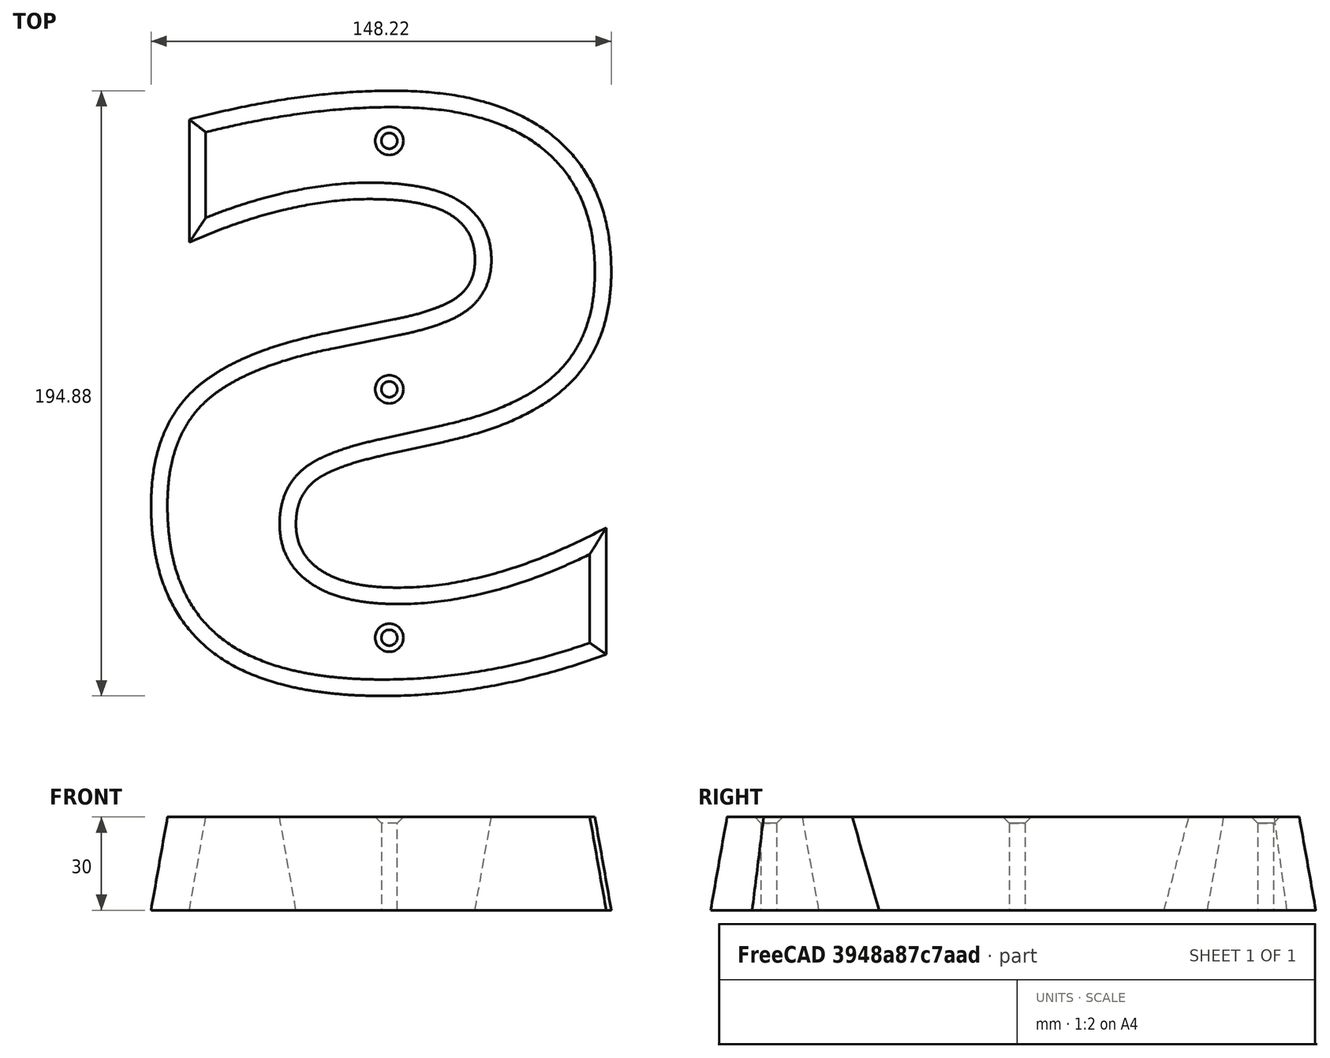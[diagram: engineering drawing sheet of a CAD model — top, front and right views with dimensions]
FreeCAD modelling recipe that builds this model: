
FCSTD DOCUMENT  (FreeCAD 0.21RUnknown)
Label: s-mirror
License: All rights reserved
LicenseURL: https://en.wikipedia.org/wiki/All_rights_reserved
objects: Part::Cylinder×3, Part::Cut×3, Part::Offset2D×2, Part::Part2DObjectPython×1, Part::Mirroring×1, Sketcher::SketchObject×1, Part::Loft×1, Part::Chamfer×1
note: 13 computed .brp shape members not serialized (recipe doc carries the construction recipe); baked Part::Feature solids carry a one-line shape summary decoded from their .brp

FEATURE [Part::Part2DObjectPython] ShapeString  # Draft 2D object (typed FeaturePython)
  FontFile = /nix/var/nix/profiles/system/sw/share/X11/fonts/DejaVuSans-Bold.ttf
  MakeFace = false
  Size = 200
  String = S
  Tracking = 0
FEATURE [Part::Mirroring] Mirror  label="ShapeString (mirrored)"
  Base = (0,0,0)
  Normal = (1,0,0)
  Source = -> ShapeString
FEATURE [Sketcher::SketchObject] Sketch  label="s-Sketch"
  FullyConstrained = false
  sketch-geometry (92):
    g0: LineSegment StartX=-154.404 StartY=181.888 StartZ=0 EndX=-154.404 EndY=142.282 EndZ=0
    g1: ArcOfCircle CenterX=-72.4025 CenterY=-127.848 CenterZ=0 NormalX=0 NormalY=0 NormalZ=1 AngleXU=0 Radius=320.406 StartAngle=1.77565 EndAngle=1.82961
    g2: ArcOfCircle CenterX=-83.2735 CenterY=-75.5247 CenterZ=0 NormalX=0 NormalY=0 NormalZ=1 AngleXU=0 Radius=266.966 StartAngle=1.7109 EndAngle=1.77565
    g3: ArcOfCircle CenterX=-86.4858 CenterY=-51.8715 CenterZ=0 NormalX=0 NormalY=0 NormalZ=1 AngleXU=0 Radius=243.096 StartAngle=1.64569 EndAngle=1.7114
    g4: ArcOfCircle CenterX=-88.7164 CenterY=-22.1421 CenterZ=0 NormalX=0 NormalY=0 NormalZ=1 AngleXU=0 Radius=213.283 StartAngle=1.5708 EndAngle=1.64569
    g5: ArcOfCircle CenterX=-88.7164 CenterY=52.2641 CenterZ=0 NormalX=0 NormalY=0 NormalZ=1 AngleXU=0 Radius=138.877 StartAngle=1.46144 EndAngle=1.5708
    g6: ArcOfCircle CenterX=-83.1389 CenterY=103.065 CenterZ=0 NormalX=0 NormalY=0 NormalZ=1 AngleXU=0 Radius=87.7708 StartAngle=1.28867 EndAngle=1.46144
    g7: ArcOfCircle CenterX=-78.3313 CenterY=119.651 CenterZ=0 NormalX=0 NormalY=0 NormalZ=1 AngleXU=0 Radius=70.5019 StartAngle=1.11122 EndAngle=1.28867
    g8: ArcOfCircle CenterX=-70.6109 CenterY=135.25 CenterZ=0 NormalX=0 NormalY=0 NormalZ=1 AngleXU=0 Radius=53.0969 StartAngle=0.876058 EndAngle=1.11122
    g9: ArcOfCircle CenterX=-67.6851 CenterY=138.761 CenterZ=0 NormalX=0 NormalY=0 NormalZ=1 AngleXU=0 Radius=48.5266 StartAngle=0.638556 EndAngle=0.876058
    g10: ArcOfCircle CenterX=-67.0907 CenterY=139.202 CenterZ=0 NormalX=0 NormalY=0 NormalZ=1 AngleXU=0 Radius=47.7863 StartAngle=0.39741 EndAngle=0.638556
    g11: ArcOfCircle CenterX=-72.8538 CenterY=136.783 CenterZ=0 NormalX=0 NormalY=0 NormalZ=1 AngleXU=0 Radius=54.0366 StartAngle=0.162609 EndAngle=0.39741
    g12: ArcOfCircle CenterX=-96.7123 CenterY=132.869 CenterZ=0 NormalX=0 NormalY=0 NormalZ=1 AngleXU=0 Radius=78.214 StartAngle=-9e-16 EndAngle=0.162609
    g13: ArcOfCircle CenterX=-88.6496 CenterY=132.869 CenterZ=0 NormalX=0 NormalY=0 NormalZ=1 AngleXU=0 Radius=70.1513 StartAngle=6.13716 EndAngle=6.28319
    g14: ArcOfCircle CenterX=-68.7218 CenterY=129.938 CenterZ=0 NormalX=0 NormalY=0 NormalZ=1 AngleXU=0 Radius=50.0091 StartAngle=5.93268 EndAngle=6.13716
    g15: ArcOfCircle CenterX=-63.2383 CenterY=127.934 CenterZ=0 NormalX=0 NormalY=0 NormalZ=1 AngleXU=0 Radius=44.1707 StartAngle=5.72359 EndAngle=5.93268
    g16: ArcOfCircle CenterX=-61.6232 CenterY=126.922 CenterZ=0 NormalX=0 NormalY=0 NormalZ=1 AngleXU=0 Radius=42.2648 StartAngle=5.50514 EndAngle=5.72359
    g17: ArcOfCircle CenterX=-65.5059 CenterY=130.769 CenterZ=0 NormalX=0 NormalY=0 NormalZ=1 AngleXU=0 Radius=47.731 StartAngle=5.29096 EndAngle=5.50482
    g18: ArcOfCircle CenterX=-78.9203 CenterY=151.308 CenterZ=0 NormalX=0 NormalY=0 NormalZ=1 AngleXU=0 Radius=72.2623 StartAngle=5.14939 EndAngle=5.29096
    g19: ArcOfCircle CenterX=-87.2378 CenterY=169.114 CenterZ=0 NormalX=0 NormalY=0 NormalZ=1 AngleXU=0 Radius=91.9148 StartAngle=5.00977 EndAngle=5.14939
    g20: ArcOfCircle CenterX=-103.93 CenterY=223.579 CenterZ=0 NormalX=0 NormalY=0 NormalZ=1 AngleXU=0 Radius=148.88 StartAngle=4.92348 EndAngle=5.00977
    g21: LineSegment StartX=-91.4849 StartY=73.8339 StartZ=0 EndX=-72.7349 EndY=78.0034 EndZ=0
    g22: ArcOfCircle CenterX=-56.162 CenterY=-85.588 CenterZ=0 NormalX=0 NormalY=0 NormalZ=1 AngleXU=-3.14159 Radius=163.288 StartAngle=4.93044 EndAngle=4.97589
    g23: ArcOfCircle CenterX=-78.6317 CenterY=-2.29803 CenterZ=0 NormalX=0 NormalY=0 NormalZ=1 AngleXU=-3.14159 Radius=77.0206 StartAngle=4.97589 EndAngle=5.07221
    g24: ArcOfCircle CenterX=-86.261 CenterY=17.9823 CenterZ=0 NormalX=0 NormalY=0 NormalZ=1 AngleXU=-3.14159 Radius=55.3527 StartAngle=5.07221 EndAngle=5.1216
    g25: ArcOfCircle CenterX=-94.4489 CenterY=36.8616 CenterZ=0 NormalX=0 NormalY=0 NormalZ=1 AngleXU=-3.14159 Radius=34.7742 StartAngle=5.1216 EndAngle=5.20021
    g26: ArcOfCircle CenterX=-97.8393 CenterY=43.2514 CenterZ=0 NormalX=0 NormalY=0 NormalZ=1 AngleXU=-3.14159 Radius=27.5408 StartAngle=5.20021 EndAngle=5.27789
    g27: ArcOfCircle CenterX=-103.946 CenterY=52.874 CenterZ=0 NormalX=0 NormalY=0 NormalZ=1 AngleXU=-3.14159 Radius=16.1439 StartAngle=5.27789 EndAngle=5.41029
    g28: ArcOfCircle CenterX=-104.376 CenterY=53.3693 CenterZ=0 NormalX=0 NormalY=0 NormalZ=1 AngleXU=-3.14159 Radius=15.488 StartAngle=5.40957 EndAngle=5.6451
    g29: ArcOfCircle CenterX=-104.632 CenterY=53.5589 CenterZ=0 NormalX=0 NormalY=0 NormalZ=1 AngleXU=-3.14159 Radius=15.1697 StartAngle=5.6451 EndAngle=5.88552
    g30: ArcOfCircle CenterX=-102.87 CenterY=52.8188 CenterZ=0 NormalX=0 NormalY=0 NormalZ=1 AngleXU=-3.14159 Radius=17.081 StartAngle=5.88552 EndAngle=6.11984
    g31: ArcOfCircle CenterX=-95.4893 CenterY=51.6023 CenterZ=0 NormalX=0 NormalY=0 NormalZ=1 AngleXU=-3.14159 Radius=24.5611 StartAngle=6.11984 EndAngle=6.28319
    g32: ArcOfCircle CenterX=-99.5529 CenterY=51.6023 CenterZ=0 NormalX=0 NormalY=0 NormalZ=1 AngleXU=-3.14159 Radius=20.4974 StartAngle=-9e-16 EndAngle=0.221382
    g33: ArcOfCircle CenterX=-104.124 CenterY=50.5736 CenterZ=0 NormalX=0 NormalY=0 NormalZ=1 AngleXU=-3.14159 Radius=15.8122 StartAngle=0.221382 EndAngle=0.507568
    g34: ArcOfCircle CenterX=-103.996 CenterY=50.6444 CenterZ=0 NormalX=0 NormalY=0 NormalZ=1 AngleXU=-3.14159 Radius=15.9579 StartAngle=0.507568 EndAngle=0.793047
    g35: ArcOfCircle CenterX=-100.328 CenterY=54.369 CenterZ=0 NormalX=0 NormalY=0 NormalZ=1 AngleXU=-3.14159 Radius=21.1854 StartAngle=0.793047 EndAngle=1.00872
    g36: ArcOfCircle CenterX=-97.6855 CenterY=58.6 CenterZ=0 NormalX=0 NormalY=0 NormalZ=1 AngleXU=-3.14159 Radius=26.1741 StartAngle=1.00943 EndAngle=1.22095
    g37: ArcOfCircle CenterX=-92.5595 CenterY=72.6496 CenterZ=0 NormalX=0 NormalY=0 NormalZ=1 AngleXU=-3.14159 Radius=41.1296 StartAngle=1.22095 EndAngle=1.35586
    g38: ArcOfCircle CenterX=-90.0842 CenterY=83.988 CenterZ=0 NormalX=0 NormalY=0 NormalZ=1 AngleXU=-3.14159 Radius=52.735 StartAngle=1.35586 EndAngle=1.48939
    g39: ArcOfCircle CenterX=-87.3322 CenterY=117.719 CenterZ=0 NormalX=0 NormalY=0 NormalZ=1 AngleXU=-3.14159 Radius=86.5777 StartAngle=1.48939 EndAngle=1.5708
    g40: ArcOfCircle CenterX=-87.3322 CenterY=135.782 CenterZ=0 NormalX=0 NormalY=0 NormalZ=1 AngleXU=-3.14159 Radius=104.641 StartAngle=1.5708 EndAngle=1.72785
    g41: ArcOfCircle CenterX=-91.5759 CenterY=162.581 CenterZ=0 NormalX=0 NormalY=0 NormalZ=1 AngleXU=-3.14159 Radius=131.774 StartAngle=1.72785 EndAngle=1.85265
    g42: ArcOfCircle CenterX=-98.6888 CenterY=187.069 CenterZ=0 NormalX=0 NormalY=0 NormalZ=1 AngleXU=-3.14159 Radius=157.274 StartAngle=1.85279 EndAngle=1.97275
    g43: ArcOfCircle CenterX=-121.083 CenterY=239.748 CenterZ=0 NormalX=0 NormalY=0 NormalZ=1 AngleXU=-3.14159 Radius=214.516 StartAngle=1.97275 EndAngle=2.06075
    g44: LineSegment StartX=-20.1342 StartY=9.62248 StartZ=0 EndX=-20.1342 EndY=50.4698 EndZ=0
    g45: ArcOfCircle CenterX=-100.994 CenterY=229.172 CenterZ=0 NormalX=0 NormalY=0 NormalZ=1 AngleXU=0 Radius=233.967 StartAngle=4.98535 EndAngle=5.06527
    g46: ArcOfCircle CenterX=-95.399 CenterY=209.186 CenterZ=0 NormalX=0 NormalY=0 NormalZ=1 AngleXU=0 Radius=213.212 StartAngle=4.89765 EndAngle=4.98535
    g47: ArcOfCircle CenterX=-92.8896 CenterY=195.31 CenterZ=0 NormalX=0 NormalY=0 NormalZ=1 AngleXU=0 Radius=199.111 StartAngle=4.80751 EndAngle=4.8981
    g48: ArcOfCircle CenterX=-91.9883 CenterY=185.862 CenterZ=0 NormalX=0 NormalY=0 NormalZ=1 AngleXU=0 Radius=189.621 StartAngle=4.71239 EndAngle=4.80751
    g49: ArcOfCircle CenterX=-91.9883 CenterY=174.795 CenterZ=0 NormalX=0 NormalY=0 NormalZ=1 AngleXU=0 Radius=178.553 StartAngle=4.66266 EndAngle=4.71239
    g50: ArcOfCircle CenterX=-94.0407 CenterY=133.559 CenterZ=0 NormalX=0 NormalY=0 NormalZ=1 AngleXU=0 Radius=137.267 StartAngle=4.59798 EndAngle=4.66266
    g51: ArcOfCircle CenterX=-95.9736 CenterY=116.739 CenterZ=0 NormalX=0 NormalY=0 NormalZ=1 AngleXU=0 Radius=120.335 StartAngle=4.53328 EndAngle=4.59798
    g52: ArcOfCircle CenterX=-100.933 CenterY=89.3496 CenterZ=0 NormalX=0 NormalY=0 NormalZ=1 AngleXU=0 Radius=92.501 StartAngle=4.44913 EndAngle=4.53328
    g53: ArcOfCircle CenterX=-105.006 CenterY=74.2344 CenterZ=0 NormalX=0 NormalY=0 NormalZ=1 AngleXU=0 Radius=76.8464 StartAngle=4.2789 EndAngle=4.44913
    g54: ArcOfCircle CenterX=-115.832 CenterY=50.8464 CenterZ=0 NormalX=0 NormalY=0 NormalZ=1 AngleXU=0 Radius=51.0746 StartAngle=4.02354 EndAngle=4.2789
    g55: ArcOfCircle CenterX=-119.371 CenterY=46.564 CenterZ=0 NormalX=0 NormalY=0 NormalZ=1 AngleXU=0 Radius=45.5189 StartAngle=3.76158 EndAngle=4.02377
    g56: ArcOfCircle CenterX=-116.053 CenterY=48.9329 CenterZ=0 NormalX=0 NormalY=0 NormalZ=1 AngleXU=0 Radius=49.5961 StartAngle=3.52072 EndAngle=3.76158
    g57: ArcOfCircle CenterX=-109.79 CenterY=51.4279 CenterZ=0 NormalX=0 NormalY=0 NormalZ=1 AngleXU=0 Radius=56.3372 StartAngle=3.40486 EndAngle=3.52072
    g58: ArcOfCircle CenterX=-97.7599 CenterY=54.6703 CenterZ=0 NormalX=0 NormalY=0 NormalZ=1 AngleXU=0 Radius=68.7968 StartAngle=3.30994 EndAngle=3.40486
    g59: ArcOfCircle CenterX=-89.3288 CenterY=56.1032 CenterZ=0 NormalX=0 NormalY=0 NormalZ=1 AngleXU=0 Radius=77.3488 StartAngle=3.21544 EndAngle=3.30994
    g60: ArcOfCircle CenterX=-67.7259 CenterY=57.7013 CenterZ=0 NormalX=0 NormalY=0 NormalZ=1 AngleXU=0 Radius=99.0107 StartAngle=3.14159 EndAngle=3.21544
    g61: ArcOfCircle CenterX=-90.033 CenterY=57.7013 CenterZ=0 NormalX=0 NormalY=0 NormalZ=1 AngleXU=0 Radius=76.7036 StartAngle=3.00239 EndAngle=3.14159
    g62: ArcOfCircle CenterX=-115.25 CenterY=61.2344 CenterZ=0 NormalX=0 NormalY=0 NormalZ=1 AngleXU=0 Radius=51.2406 StartAngle=2.79443 EndAngle=3.00239
    g63: ArcOfCircle CenterX=-122.61 CenterY=63.8975 CenterZ=0 NormalX=0 NormalY=0 NormalZ=1 AngleXU=0 Radius=43.4135 StartAngle=2.58012 EndAngle=2.79443
    g64: ArcOfCircle CenterX=-126.312 CenterY=66.2259 CenterZ=0 NormalX=0 NormalY=0 NormalZ=1 AngleXU=0 Radius=39.0402 StartAngle=2.34203 EndAngle=2.58012
    g65: ArcOfCircle CenterX=-124.393 CenterY=64.2517 CenterZ=0 NormalX=0 NormalY=0 NormalZ=1 AngleXU=0 Radius=41.7935 StartAngle=2.2246 EndAngle=2.34203
    g66: ArcOfCircle CenterX=-116.78 CenterY=54.3163 CenterZ=0 NormalX=0 NormalY=0 NormalZ=1 AngleXU=0 Radius=54.3101 StartAngle=2.13418 EndAngle=2.2246
    g67: ArcOfCircle CenterX=-112.344 CenterY=47.2934 CenterZ=0 NormalX=0 NormalY=0 NormalZ=1 AngleXU=0 Radius=62.6168 StartAngle=2.04409 EndAngle=2.13418
    g68: ArcOfCircle CenterX=-102.724 CenterY=28.5093 CenterZ=0 NormalX=0 NormalY=0 NormalZ=1 AngleXU=0 Radius=83.7208 StartAngle=1.97669 EndAngle=2.04409
    g69: ArcOfCircle CenterX=-93.9943 CenterY=8.19599 CenterZ=0 NormalX=0 NormalY=0 NormalZ=1 AngleXU=0 Radius=105.831 StartAngle=1.84444 EndAngle=1.97669
    g70: ArcOfCircle CenterX=-72.263 CenterY=-69.226 CenterZ=0 NormalX=0 NormalY=0 NormalZ=1 AngleXU=0 Radius=186.245 StartAngle=1.76922 EndAngle=1.84444
    g71: LineSegment StartX=-88.3389 StartY=117.525 StartZ=0 EndX=-108.977 EndY=113.364 EndZ=0
    g72: ArcOfCircle CenterX=-116.046 CenterY=252.222 CenterZ=0 NormalX=0 NormalY=0 NormalZ=1 AngleXU=-3.14159 Radius=137.517 StartAngle=1.77366 EndAngle=1.82055
    g73: ArcOfCircle CenterX=-99.2236 CenterY=186.273 CenterZ=0 NormalX=0 NormalY=0 NormalZ=1 AngleXU=-3.14159 Radius=69.456 StartAngle=1.82055 EndAngle=1.91332
    g74: ArcOfCircle CenterX=-92.9649 CenterY=168.721 CenterZ=0 NormalX=0 NormalY=0 NormalZ=1 AngleXU=-3.14159 Radius=50.8215 StartAngle=1.91332 EndAngle=2.00044
    g75: ArcOfCircle CenterX=-80.315 CenterY=141.113 CenterZ=0 NormalX=0 NormalY=0 NormalZ=1 AngleXU=-3.14159 Radius=20.4533 StartAngle=2.00044 EndAngle=2.21621
    g76: ArcOfCircle CenterX=-76.9918 CenterY=136.658 CenterZ=0 NormalX=0 NormalY=0 NormalZ=1 AngleXU=-3.14159 Radius=14.8956 StartAngle=2.21789 EndAngle=2.44093
    g77: ArcOfCircle CenterX=-75.4462 CenterY=135.354 CenterZ=0 NormalX=0 NormalY=0 NormalZ=1 AngleXU=-3.14159 Radius=12.8736 StartAngle=2.44093 EndAngle=2.69864
    g78: ArcOfCircle CenterX=-76.1169 CenterY=135.672 CenterZ=0 NormalX=0 NormalY=0 NormalZ=1 AngleXU=-3.14159 Radius=13.616 StartAngle=2.69864 EndAngle=2.95292
    g79: ArcOfCircle CenterX=-80.8115 CenterY=136.569 CenterZ=0 NormalX=0 NormalY=0 NormalZ=1 AngleXU=-3.14159 Radius=18.3954 StartAngle=2.95292 EndAngle=3.14159
    g80: ArcOfCircle CenterX=-84.0066 CenterY=136.569 CenterZ=0 NormalX=0 NormalY=0 NormalZ=1 AngleXU=-3.14159 Radius=21.5905 StartAngle=3.14159 EndAngle=3.35291
    g81: ArcOfCircle CenterX=-77.826 CenterY=137.895 CenterZ=0 NormalX=0 NormalY=0 NormalZ=1 AngleXU=-3.14159 Radius=15.2693 StartAngle=3.35291 EndAngle=3.6506
    g82: ArcOfCircle CenterX=-77.2817 CenterY=138.198 CenterZ=0 NormalX=0 NormalY=0 NormalZ=1 AngleXU=-3.14159 Radius=14.646 StartAngle=3.6506 EndAngle=3.95183
    g83: ArcOfCircle CenterX=-80.0331 CenterY=135.307 CenterZ=0 NormalX=0 NormalY=0 NormalZ=1 AngleXU=-3.14159 Radius=18.6374 StartAngle=3.95183 EndAngle=4.18923
    g84: ArcOfCircle CenterX=-83.3648 CenterY=129.53 CenterZ=0 NormalX=0 NormalY=0 NormalZ=1 AngleXU=-3.14159 Radius=25.3058 StartAngle=4.18923 EndAngle=4.41057
    g85: ArcOfCircle CenterX=-90.0743 CenterY=107.979 CenterZ=0 NormalX=0 NormalY=0 NormalZ=1 AngleXU=-3.14159 Radius=47.8773 StartAngle=4.41057 EndAngle=4.52791
    g86: ArcOfCircle CenterX=-93.0401 CenterY=92.0853 CenterZ=0 NormalX=0 NormalY=0 NormalZ=1 AngleXU=-3.14159 Radius=64.0455 StartAngle=4.52791 EndAngle=4.64629
    g87: ArcOfCircle CenterX=-96.3926 CenterY=41.4375 CenterZ=0 NormalX=0 NormalY=0 NormalZ=1 AngleXU=-3.14159 Radius=114.804 StartAngle=4.64629 EndAngle=4.71239
    g88: ArcOfCircle CenterX=-96.3926 CenterY=51.8575 CenterZ=0 NormalX=0 NormalY=0 NormalZ=1 AngleXU=-3.14159 Radius=104.384 StartAngle=4.71239 EndAngle=4.84693
    g89: ArcOfCircle CenterX=-91.6103 CenterY=16.527 CenterZ=0 NormalX=0 NormalY=0 NormalZ=1 AngleXU=-3.14159 Radius=140.037 StartAngle=4.84693 EndAngle=4.94729
    g90: ArcOfCircle CenterX=-88.3502 CenterY=2.54692 CenterZ=0 NormalX=0 NormalY=0 NormalZ=1 AngleXU=-3.14159 Radius=154.392 StartAngle=4.94675 EndAngle=5.05036
    g91: ArcOfCircle CenterX=-75.2346 CenterY=-34.7704 CenterZ=0 NormalX=0 NormalY=0 NormalZ=1 AngleXU=-3.14159 Radius=193.947 StartAngle=5.05036 EndAngle=5.13287
  constraints (94):
    c: Vertical(g0)
    c: Coincident(g0,g1)
    c: Coincident(g1,g2)
    c: Coincident(g2,g3)
    c: Coincident(g3,g4)
    c: Coincident(g4,g5)
    c: Coincident(g5,g6)
    c: Coincident(g6,g7)
    c: Coincident(g7,g8)
    c: Coincident(g8,g9)
    c: Coincident(g9,g10)
    c: Coincident(g10,g11)
    c: Coincident(g11,g12)
    c: Coincident(g12,g13)
    c: Coincident(g13,g14)
    c: Coincident(g14,g15)
    c: Coincident(g15,g16)
    c: Coincident(g16,g17)
    c: Coincident(g17,g18)
    c: Coincident(g18,g19)
    c: Coincident(g19,g20)
    c: Coincident(g20,g21)
    c: Coincident(g21,g22)
    c: Coincident(g22,g23)
    c: Coincident(g23,g24)
    c: Coincident(g24,g25)
    c: Coincident(g25,g26)
    c: Coincident(g26,g27)
    c: Coincident(g27,g28)
    c: Coincident(g28,g29)
    c: Coincident(g29,g30)
    c: Coincident(g30,g31)
    c: Coincident(g31,g32)
    c: Coincident(g32,g33)
    c: Coincident(g33,g34)
    c: Coincident(g34,g35)
    c: Coincident(g35,g36)
    c: Coincident(g36,g37)
    c: Coincident(g37,g38)
    c: Coincident(g38,g39)
    c: Coincident(g39,g40)
    c: Coincident(g40,g41)
    c: Coincident(g41,g42)
    c: Coincident(g42,g43)
    c: Coincident(g43,g44)
    c: Vertical(g44)
    c: Coincident(g44,g45)
    c: Coincident(g45,g46)
    c: Coincident(g46,g47)
    c: Coincident(g47,g48)
    c: Coincident(g48,g49)
    c: Coincident(g49,g50)
    c: Coincident(g50,g51)
    c: Coincident(g51,g52)
    c: Coincident(g52,g53)
    c: Coincident(g53,g54)
    c: Coincident(g54,g55)
    c: Coincident(g55,g56)
    c: Coincident(g56,g57)
    c: Coincident(g57,g58)
    c: Coincident(g58,g59)
    c: Coincident(g59,g60)
    c: Coincident(g60,g61)
    c: Coincident(g61,g62)
    c: Coincident(g62,g63)
    c: Coincident(g63,g64)
    c: Coincident(g64,g65)
    c: Coincident(g65,g66)
    c: Coincident(g66,g67)
    c: Coincident(g67,g68)
    c: Coincident(g68,g69)
    c: Coincident(g69,g70)
    c: Coincident(g70,g71)
    c: Coincident(g71,g72)
    c: Coincident(g72,g73)
    c: Coincident(g73,g74)
    c: Coincident(g74,g75)
    c: Coincident(g75,g76)
    c: Coincident(g76,g77)
    c: Coincident(g77,g78)
    c: Coincident(g78,g79)
    c: Coincident(g79,g80)
    c: Coincident(g80,g81)
    c: Coincident(g81,g82)
    c: Coincident(g82,g83)
    c: Coincident(g83,g84)
    c: Coincident(g84,g85)
    c: Coincident(g85,g86)
    c: Coincident(g86,g87)
    c: Coincident(g87,g88)
    c: Coincident(g88,g89)
    c: Coincident(g89,g90)
    c: Coincident(g90,g91)
    c: Coincident(g91,g0)
FEATURE [Part::Offset2D] Offset2D
  Fill = false
  Intersection = false
  Join = 0
  Mode = 1
  SelfIntersection = false
  Source = -> Sketch
  Value = -0.01
FEATURE [Part::Offset2D] Offset2D001
  Fill = false
  Intersection = false
  Join = 0
  Mode = 1
  Placement = pos=(0,0,30) rot=(0,0,1;0rad)
  SelfIntersection = false
  Source = -> Sketch
  Value = -5.28981
  expr: Value = -.Placement.Base.z * tan(10)
FEATURE [Part::Loft] Loft
  Closed = false
  MaxDegree = 5
  Ruled = false
  Sections = -> [Offset2D,Offset2D001]
  Solid = true
FEATURE [Part::Cylinder] Cylinder
  Angle = 360
  AttacherType = Attacher::AttachEngine3D
  FirstAngle = 0
  Height = 40
  Placement = pos=(-90,15,0) rot=(0,0,1;0rad)
  Radius = 2.55
  SecondAngle = 0
FEATURE [Part::Cylinder] Cylinder001
  Angle = 360
  AttacherType = Attacher::AttachEngine3D
  FirstAngle = 0
  Height = 40
  Placement = pos=(-90,95,0) rot=(0,0,1;0rad)
  Radius = 2.55
  SecondAngle = 0
FEATURE [Part::Cylinder] Cylinder002
  Angle = 360
  AttacherType = Attacher::AttachEngine3D
  FirstAngle = 0
  Height = 40
  Placement = pos=(-90,175,0) rot=(0,0,1;0rad)
  Radius = 2.55
  SecondAngle = 0
FEATURE [Part::Cut] Cut
  Base = -> Loft
  Tool = -> Cylinder
FEATURE [Part::Cut] Cut001
  Base = -> Cut
  Tool = -> Cylinder001
FEATURE [Part::Cut] Cut002
  Base = -> Cut001
  Tool = -> Cylinder002
FEATURE [Part::Chamfer] Chamfer
  Base = -> Cut002
  Edges = 3 edges r=2: [Edge209,Edge210,Edge211]
